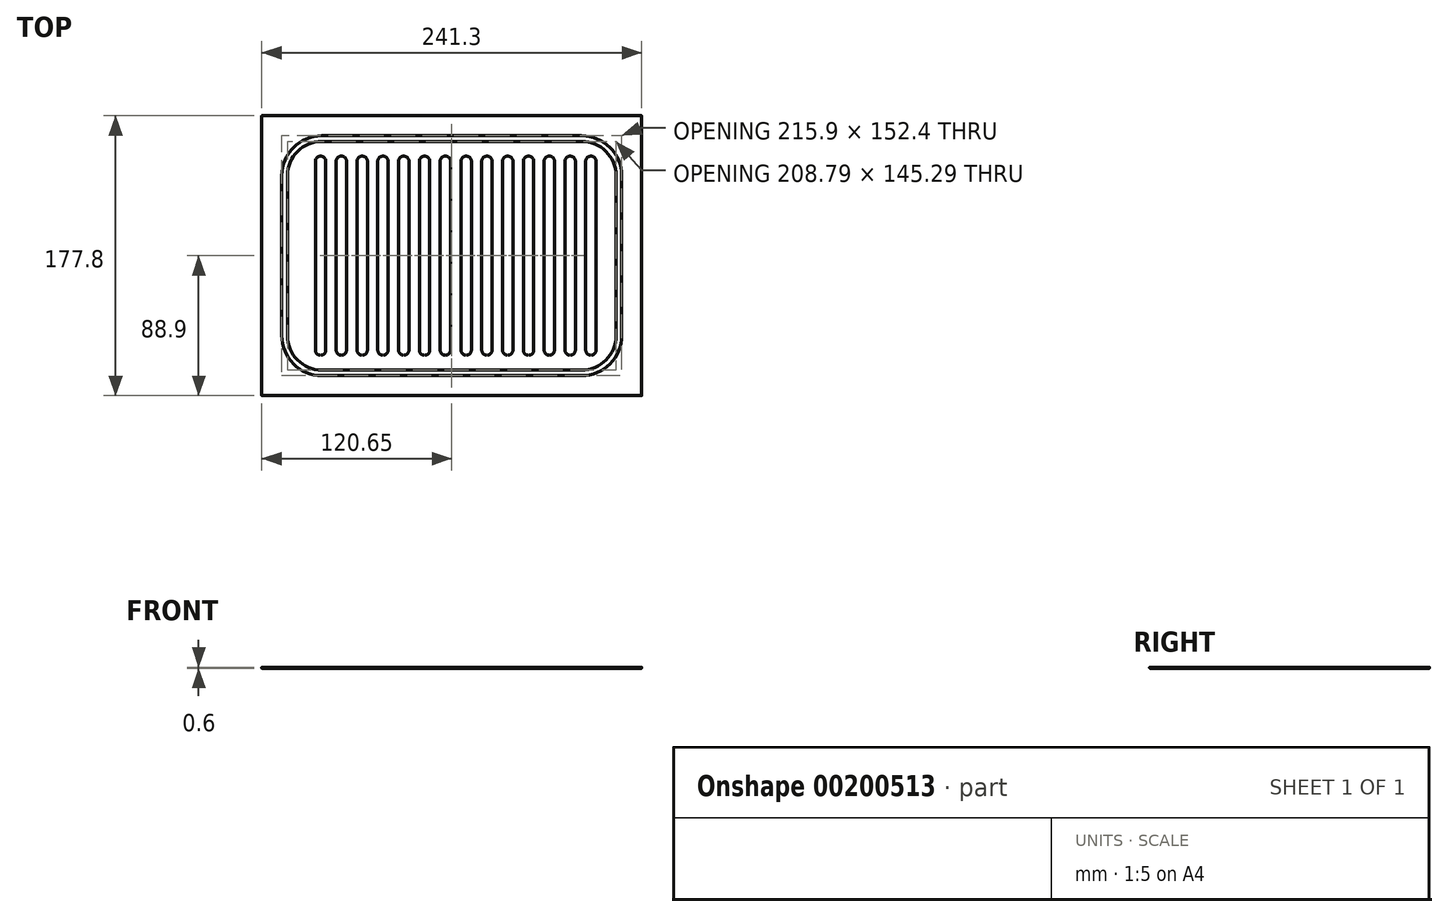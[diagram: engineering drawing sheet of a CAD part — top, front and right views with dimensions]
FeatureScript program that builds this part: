
annotation { "Feature Type Name" : "Feature", "Feature Type Description" : "" }
export const myFeature = defineFeature(function(context is Context, id is Id, definition is map)
    precondition{}
    {
        {
            var Q0;
            Q0=qCreatedBy(makeId("Top.planeOp"),FACE);
            var sketch = newSketch(context, id + "F0", { "sketchPlane" : qUnion([Q0])});
            skLineSegment(sketch, "E0.bottom", {"start": v(0, 177.8) * mm, "end": v(241.3, 177.8) * mm});
            skLineSegment(sketch, "E0.top", {"start": v(0, 0) * mm, "end": v(241.3, 0) * mm});
            skLineSegment(sketch, "E0.left", {"start": v(0, 177.8) * mm, "end": v(0, 0) * mm});
            skLineSegment(sketch, "E0.right", {"start": v(241.3, 177.8) * mm, "end": v(241.3, 0) * mm});
            skSolve(sketch);
        }
        {
            assignVariable(context, id + "F1", {"name" : "thickness", "anyValue" : .6});
        }
        {
            var Q0;
            Q0=makeQuery(id+"F0.imprint","IMPRINT",FACE,{"disambiguationData":[TD([[makeQuery(id+"F0.imprint","IMPRINT",EDGE,{"derivedFrom":sQuery(id+"F0.wireOp",EDGE,"E0.bottom")}),-1.0]])]});
            extrude(context, id + "F2", {"entities" : qUnion([Q0]), "depth" : (getVariable(context, 'thickness')) * mm});
        }
        {
            var Q0;
            Q0=makeQuery(id+"F2.opExtrude","CAP_FACE",FACE,{"disambiguationData":[OSD([sQuery(id+"F0.wireOp",EDGE,"E0.bottom"),sQuery(id+"F0.wireOp",EDGE,"E0.top"),sQuery(id+"F0.wireOp",EDGE,"E0.left"),sQuery(id+"F0.wireOp",EDGE,"E0.right"),sQuery(id+"F0.wireOp",EDGE,"lCrXFNj8-C2Ty-3Pfg-9sqa-s09L6QDRjWCV"),sQuery(id+"F0.wireOp",EDGE,"ff08c771-16cc-4d6c-ab3f-2ea9cd5ef540.0.1.0"),sQuery(id+"F0.wireOp",EDGE,"ff08c771-16cc-4d6c-ab3f-2ea9cd5ef540.0.2.0"),sQuery(id+"F0.wireOp",EDGE,"ff08c771-16cc-4d6c-ab3f-2ea9cd5ef540.1.0.0"),sQuery(id+"F0.wireOp",EDGE,"ff08c771-16cc-4d6c-ab3f-2ea9cd5ef540.1.1.0"),sQuery(id+"F0.wireOp",EDGE,"ff08c771-16cc-4d6c-ab3f-2ea9cd5ef540.1.2.0"),sQuery(id+"F0.wireOp",EDGE,"ff08c771-16cc-4d6c-ab3f-2ea9cd5ef540.2.0.0"),sQuery(id+"F0.wireOp",EDGE,"ff08c771-16cc-4d6c-ab3f-2ea9cd5ef540.2.1.0"),sQuery(id+"F0.wireOp",EDGE,"ff08c771-16cc-4d6c-ab3f-2ea9cd5ef540.2.2.0")])],"isStart":false});
            var sketch = newSketch(context, id + "F3", { "sketchPlane" : qUnion([Q0])});
            skLineSegment(sketch, "E1.0", {"start": v(203.2, 165.1) * mm, "end": v(38.1, 165.1) * mm});
            skLineSegment(sketch, "E1.1", {"start": v(228.6, 38.1) * mm, "end": v(228.6, 139.7) * mm});
            skLineSegment(sketch, "E1.2", {"start": v(38.1, 12.7) * mm, "end": v(203.2, 12.7) * mm});
            skLineSegment(sketch, "E1.3", {"start": v(12.7, 139.7) * mm, "end": v(12.7, 38.1) * mm});
            skArc(sketch, "E2.filletArc", {"start": v(38.1, 165.1) * mm, "mid": v(20.14, 157.66) * mm, "end": v(12.7, 139.7) * mm});
            skArc(sketch, "E3.filletArc", {"start": v(12.7, 38.1) * mm, "mid": v(20.14, 20.14) * mm, "end": v(38.1, 12.7) * mm});
            skArc(sketch, "E4.filletArc", {"start": v(203.2, 12.7) * mm, "mid": v(221.16, 20.14) * mm, "end": v(228.6, 38.1) * mm});
            skArc(sketch, "E5.filletArc", {"start": v(228.6, 139.7) * mm, "mid": v(221.16, 157.66) * mm, "end": v(203.2, 165.1) * mm});
            skLineSegment(sketch, "E6.0", {"start": v(16.26, 139.7) * mm, "end": v(16.26, 38.1) * mm});
            skLineSegment(sketch, "E7.0", {"start": v(38.1, 16.26) * mm, "end": v(203.2, 16.26) * mm});
            skLineSegment(sketch, "E8.0", {"start": v(225.04, 38.1) * mm, "end": v(225.04, 139.7) * mm});
            skLineSegment(sketch, "E9.0", {"start": v(203.2, 161.54) * mm, "end": v(38.1, 161.54) * mm});
            skArc(sketch, "E10.0", {"start": v(16.26, 38.1) * mm, "mid": v(22.65, 22.65) * mm, "end": v(38.1, 16.26) * mm});
            skArc(sketch, "E11.0", {"start": v(203.2, 16.26) * mm, "mid": v(218.65, 22.65) * mm, "end": v(225.04, 38.1) * mm});
            skArc(sketch, "E12.0", {"start": v(225.04, 139.7) * mm, "mid": v(218.65, 155.15) * mm, "end": v(203.2, 161.54) * mm});
            skArc(sketch, "E13.0", {"start": v(38.1, 161.54) * mm, "mid": v(22.65, 155.15) * mm, "end": v(16.26, 139.7) * mm});
            skSolve(sketch);
        }
        {
            assignVariable(context, id + "F4", {"name" : "groove_depth", "anyValue" : .15});
        }
        {
            var Q0;
            Q0=makeQuery(id+"F3.imprint","IMPRINT",FACE,{"disambiguationData":[TD([[makeQuery(id+"F3.imprint","IMPRINT",EDGE,{"derivedFrom":sQuery(id+"F3.wireOp",EDGE,"E1.0")}),1.0]])]});
            extrude(context, id + "F5", {"entities" : qUnion([Q0]), "operationType" : NewBodyOperationType.REMOVE, "oppositeDirection" : true, "depth" : (getVariable(context, 'groove_depth')) * mm});
        }
        {
            var Q0;
            Q0=makeQuery(id+"F2.opExtrude","CAP_FACE",FACE,{"disambiguationData":[OSD([sQuery(id+"F0.wireOp",EDGE,"E0.bottom"),sQuery(id+"F0.wireOp",EDGE,"E0.top"),sQuery(id+"F0.wireOp",EDGE,"E0.left"),sQuery(id+"F0.wireOp",EDGE,"E0.right")])],"isStart":true});
            var sketch = newSketch(context, id + "F6", { "sketchPlane" : qUnion([Q0])});
            skLineSegment(sketch, "E14.0", {"start": v(203.2, -12.7) * mm, "end": v(38.1, -12.7) * mm});
            skLineSegment(sketch, "E14.1", {"start": v(228.6, -139.7) * mm, "end": v(228.6, -38.1) * mm});
            skLineSegment(sketch, "E14.2", {"start": v(38.1, -165.1) * mm, "end": v(203.2, -165.1) * mm});
            skLineSegment(sketch, "E14.3", {"start": v(12.7, -38.1) * mm, "end": v(12.7, -139.7) * mm});
            skArc(sketch, "E15.filletArc", {"start": v(38.1, -12.7) * mm, "mid": v(20.14, -20.14) * mm, "end": v(12.7, -38.1) * mm});
            skArc(sketch, "E16.filletArc", {"start": v(12.7, -139.7) * mm, "mid": v(20.14, -157.66) * mm, "end": v(38.1, -165.1) * mm});
            skArc(sketch, "E17.filletArc", {"start": v(203.2, -165.1) * mm, "mid": v(221.16, -157.66) * mm, "end": v(228.6, -139.7) * mm});
            skArc(sketch, "E18.filletArc", {"start": v(228.6, -38.1) * mm, "mid": v(221.16, -20.14) * mm, "end": v(203.2, -12.7) * mm});
            skLineSegment(sketch, "E19.0", {"start": v(16.26, -38.1) * mm, "end": v(16.26, -139.7) * mm});
            skLineSegment(sketch, "E20.0", {"start": v(38.1, -161.54) * mm, "end": v(203.2, -161.54) * mm});
            skLineSegment(sketch, "E21.0", {"start": v(225.04, -139.7) * mm, "end": v(225.04, -38.1) * mm});
            skLineSegment(sketch, "E22.0", {"start": v(203.2, -16.26) * mm, "end": v(38.1, -16.26) * mm});
            skArc(sketch, "E23.0", {"start": v(16.26, -139.7) * mm, "mid": v(22.65, -155.15) * mm, "end": v(38.1, -161.54) * mm});
            skArc(sketch, "E24.0", {"start": v(203.2, -161.54) * mm, "mid": v(218.65, -155.15) * mm, "end": v(225.04, -139.7) * mm});
            skArc(sketch, "E25.0", {"start": v(225.04, -38.1) * mm, "mid": v(218.65, -22.65) * mm, "end": v(203.2, -16.26) * mm});
            skArc(sketch, "E26.0", {"start": v(38.1, -16.26) * mm, "mid": v(22.65, -22.65) * mm, "end": v(16.26, -38.1) * mm});
            skSolve(sketch);
        }
        {
            var Q0;
            Q0 = qSketchRegion(id + "F6", true);
            extrude(context, id + "F7", {"entities" : qUnion([Q0]), "operationType" : NewBodyOperationType.REMOVE, "oppositeDirection" : true, "depth" : (getVariable(context, 'groove_depth')) * mm});
        }
        {
            var Q0;
            Q0=makeQuery(id+"F2.opExtrude","CAP_FACE",FACE,{"disambiguationData":[OSD([sQuery(id+"F0.wireOp",EDGE,"E0.bottom"),sQuery(id+"F0.wireOp",EDGE,"E0.top"),sQuery(id+"F0.wireOp",EDGE,"E0.left"),sQuery(id+"F0.wireOp",EDGE,"E0.right")])],"isStart":true});
            var sketch = newSketch(context, id + "F8", { "sketchPlane" : qUnion([Q0])});
            skLineSegment(sketch, "E27", {"start": v(205.74, -148.84) * mm, "end": v(205.74, -28.96) * mm});
            skLineSegment(sketch, "E28.0", {"start": v(212.34, -148.84) * mm, "end": v(212.34, -28.96) * mm});
            skArc(sketch, "E29", {"start": v(212.34, -28.96) * mm, "mid": v(209.04, -25.65) * mm, "end": v(205.74, -28.96) * mm});
            skArc(sketch, "E30", {"start": v(205.74, -148.84) * mm, "mid": v(209.04, -152.15) * mm, "end": v(212.34, -148.84) * mm});
            skArc(sketch, "E31.1.0.0", {"start": v(199.14, -28.96) * mm, "mid": v(195.83, -25.65) * mm, "end": v(192.53, -28.96) * mm});
            skArc(sketch, "E31.1.0.1", {"start": v(192.53, -148.84) * mm, "mid": v(195.83, -152.15) * mm, "end": v(199.14, -148.84) * mm});
            skLineSegment(sketch, "E31.1.0.2", {"start": v(199.14, -148.84) * mm, "end": v(199.14, -28.96) * mm});
            skLineSegment(sketch, "E31.1.0.3", {"start": v(192.53, -148.84) * mm, "end": v(192.53, -28.96) * mm});
            skArc(sketch, "E31.2.0.0", {"start": v(185.93, -28.96) * mm, "mid": v(182.63, -25.65) * mm, "end": v(179.32, -28.96) * mm});
            skArc(sketch, "E31.2.0.1", {"start": v(179.32, -148.84) * mm, "mid": v(182.63, -152.15) * mm, "end": v(185.93, -148.84) * mm});
            skLineSegment(sketch, "E31.2.0.2", {"start": v(185.93, -148.84) * mm, "end": v(185.93, -28.96) * mm});
            skLineSegment(sketch, "E31.2.0.3", {"start": v(179.32, -148.84) * mm, "end": v(179.32, -28.96) * mm});
            skArc(sketch, "E31.3.0.0", {"start": v(172.72, -28.96) * mm, "mid": v(169.42, -25.65) * mm, "end": v(166.12, -28.96) * mm});
            skArc(sketch, "E31.3.0.1", {"start": v(166.12, -148.84) * mm, "mid": v(169.42, -152.15) * mm, "end": v(172.72, -148.84) * mm});
            skLineSegment(sketch, "E31.3.0.2", {"start": v(172.72, -148.84) * mm, "end": v(172.72, -28.96) * mm});
            skLineSegment(sketch, "E31.3.0.3", {"start": v(166.12, -148.84) * mm, "end": v(166.12, -28.96) * mm});
            skLineSegment(sketch, "E31.direction1", {"start": v(205.74, -148.84) * mm, "end": v(192.53, -148.84) * mm, "construction": true});
            skArc(sketch, "E32.0.4.0", {"start": v(159.51, -28.96) * mm, "mid": v(156.2, -25.65) * mm, "end": v(152.9, -28.96) * mm});
            skArc(sketch, "E32.4.4.0", {"start": v(152.9, -148.84) * mm, "mid": v(156.2, -152.15) * mm, "end": v(159.51, -148.84) * mm});
            skLineSegment(sketch, "E32.8.4.0", {"start": v(159.51, -148.84) * mm, "end": v(159.51, -28.96) * mm});
            skLineSegment(sketch, "E32.11.4.0", {"start": v(152.9, -148.84) * mm, "end": v(152.9, -28.96) * mm});
            skArc(sketch, "E32.0.5.0", {"start": v(146.3, -28.96) * mm, "mid": v(143, -25.65) * mm, "end": v(139.7, -28.96) * mm});
            skArc(sketch, "E32.4.5.0", {"start": v(139.7, -148.84) * mm, "mid": v(143, -152.15) * mm, "end": v(146.3, -148.84) * mm});
            skLineSegment(sketch, "E32.8.5.0", {"start": v(146.3, -148.84) * mm, "end": v(146.3, -28.96) * mm});
            skLineSegment(sketch, "E32.11.5.0", {"start": v(139.7, -148.84) * mm, "end": v(139.7, -28.96) * mm});
            skArc(sketch, "E32.0.6.0", {"start": v(133.1, -28.96) * mm, "mid": v(129.8, -25.65) * mm, "end": v(126.5, -28.96) * mm});
            skArc(sketch, "E32.4.6.0", {"start": v(126.5, -148.84) * mm, "mid": v(129.8, -152.15) * mm, "end": v(133.1, -148.84) * mm});
            skLineSegment(sketch, "E32.8.6.0", {"start": v(133.1, -148.84) * mm, "end": v(133.1, -28.96) * mm});
            skLineSegment(sketch, "E32.11.6.0", {"start": v(126.5, -148.84) * mm, "end": v(126.5, -28.96) * mm});
            skArc(sketch, "E32.0.7.0", {"start": v(119.89, -28.96) * mm, "mid": v(116.59, -25.65) * mm, "end": v(113.28, -28.96) * mm});
            skArc(sketch, "E32.4.7.0", {"start": v(113.28, -148.84) * mm, "mid": v(116.59, -152.15) * mm, "end": v(119.89, -148.84) * mm});
            skLineSegment(sketch, "E32.8.7.0", {"start": v(119.89, -148.84) * mm, "end": v(119.89, -28.96) * mm});
            skLineSegment(sketch, "E32.11.7.0", {"start": v(113.28, -148.84) * mm, "end": v(113.28, -28.96) * mm});
            skArc(sketch, "E32.0.8.0", {"start": v(106.68, -28.96) * mm, "mid": v(103.38, -25.65) * mm, "end": v(100.08, -28.96) * mm});
            skArc(sketch, "E32.4.8.0", {"start": v(100.08, -148.84) * mm, "mid": v(103.38, -152.15) * mm, "end": v(106.68, -148.84) * mm});
            skLineSegment(sketch, "E32.8.8.0", {"start": v(106.68, -148.84) * mm, "end": v(106.68, -28.96) * mm});
            skLineSegment(sketch, "E32.11.8.0", {"start": v(100.08, -148.84) * mm, "end": v(100.08, -28.96) * mm});
            skArc(sketch, "E32.0.9.0", {"start": v(93.47, -28.96) * mm, "mid": v(90.17, -25.65) * mm, "end": v(86.87, -28.96) * mm});
            skArc(sketch, "E32.4.9.0", {"start": v(86.87, -148.84) * mm, "mid": v(90.17, -152.15) * mm, "end": v(93.47, -148.84) * mm});
            skLineSegment(sketch, "E32.8.9.0", {"start": v(93.47, -148.84) * mm, "end": v(93.47, -28.96) * mm});
            skLineSegment(sketch, "E32.11.9.0", {"start": v(86.87, -148.84) * mm, "end": v(86.87, -28.96) * mm});
            skArc(sketch, "E32.0.10.0", {"start": v(80.26, -28.96) * mm, "mid": v(76.96, -25.65) * mm, "end": v(73.66, -28.96) * mm});
            skArc(sketch, "E32.4.10.0", {"start": v(73.66, -148.84) * mm, "mid": v(76.96, -152.15) * mm, "end": v(80.26, -148.84) * mm});
            skLineSegment(sketch, "E32.8.10.0", {"start": v(80.26, -148.84) * mm, "end": v(80.26, -28.96) * mm});
            skLineSegment(sketch, "E32.11.10.0", {"start": v(73.66, -148.84) * mm, "end": v(73.66, -28.96) * mm});
            skArc(sketch, "E32.0.11.0", {"start": v(67.06, -28.96) * mm, "mid": v(63.75, -25.65) * mm, "end": v(60.45, -28.96) * mm});
            skArc(sketch, "E32.4.11.0", {"start": v(60.45, -148.84) * mm, "mid": v(63.75, -152.15) * mm, "end": v(67.06, -148.84) * mm});
            skLineSegment(sketch, "E32.8.11.0", {"start": v(67.06, -148.84) * mm, "end": v(67.06, -28.96) * mm});
            skLineSegment(sketch, "E32.11.11.0", {"start": v(60.45, -148.84) * mm, "end": v(60.45, -28.96) * mm});
            skArc(sketch, "E33.0.12.0", {"start": v(53.85, -28.96) * mm, "mid": v(50.55, -25.65) * mm, "end": v(47.24, -28.96) * mm});
            skArc(sketch, "E33.4.12.0", {"start": v(47.24, -148.84) * mm, "mid": v(50.55, -152.15) * mm, "end": v(53.85, -148.84) * mm});
            skLineSegment(sketch, "E33.8.12.0", {"start": v(53.85, -148.84) * mm, "end": v(53.85, -28.96) * mm});
            skLineSegment(sketch, "E33.11.12.0", {"start": v(47.24, -148.84) * mm, "end": v(47.24, -28.96) * mm});
            skArc(sketch, "E33.0.13.0", {"start": v(40.64, -28.96) * mm, "mid": v(37.34, -25.65) * mm, "end": v(34.04, -28.96) * mm});
            skArc(sketch, "E33.4.13.0", {"start": v(34.04, -148.84) * mm, "mid": v(37.34, -152.15) * mm, "end": v(40.64, -148.84) * mm});
            skLineSegment(sketch, "E33.8.13.0", {"start": v(40.64, -148.84) * mm, "end": v(40.64, -28.96) * mm});
            skLineSegment(sketch, "E33.11.13.0", {"start": v(34.04, -148.84) * mm, "end": v(34.04, -28.96) * mm});
            skSolve(sketch);
        }
        {
            var Q0;
            Q0 = qSketchRegion(id + "F8", true);
            extrude(context, id + "F9", {"entities" : qUnion([Q0]), "operationType" : NewBodyOperationType.REMOVE, "endBound" : BoundingType.THROUGH_ALL, "oppositeDirection" : true, "depth" : 25.4 * mm});
        }
        {
            assignVariable(context, id + "F10", {"name" : "slot_radius", "anyValue" : 0.05});
        }
        {
            var Q0;
            Q0=makeQuery(id+"F9.boolean.opBoolean","INTERSECT",EDGE,{"derivedFrom":[makeQuery(id+"F5.boolean.opBoolean","SPLIT",FACE,{"disambiguationData":[TD([makeQuery(id+"F5.opExtrude","SWEPT_FACE",FACE,{"disambiguationData":[OSD([sQuery(id+"F3.wireOp",EDGE,"E6.0")])]})])],"derivedFrom":makeQuery(id+"F2.opExtrude","CAP_FACE",FACE,{"disambiguationData":[OSD([sQuery(id+"F0.wireOp",EDGE,"E0.bottom"),sQuery(id+"F0.wireOp",EDGE,"E0.top"),sQuery(id+"F0.wireOp",EDGE,"E0.left"),sQuery(id+"F0.wireOp",EDGE,"E0.right")])],"isStart":false})}),makeQuery(id+"F9.opExtrude","SWEPT_FACE",FACE,{"disambiguationData":[OSD([sQuery(id+"F8.wireOp",EDGE,"E33.11.13.0")])]})]});
            var Q1;
            Q1=makeQuery(id+"F9.boolean.opBoolean","INTERSECT",EDGE,{"derivedFrom":[makeQuery(id+"F5.boolean.opBoolean","SPLIT",FACE,{"disambiguationData":[TD([makeQuery(id+"F5.opExtrude","SWEPT_FACE",FACE,{"disambiguationData":[OSD([sQuery(id+"F3.wireOp",EDGE,"E6.0")])]})])],"derivedFrom":makeQuery(id+"F2.opExtrude","CAP_FACE",FACE,{"disambiguationData":[OSD([sQuery(id+"F0.wireOp",EDGE,"E0.bottom"),sQuery(id+"F0.wireOp",EDGE,"E0.top"),sQuery(id+"F0.wireOp",EDGE,"E0.left"),sQuery(id+"F0.wireOp",EDGE,"E0.right")])],"isStart":false})}),makeQuery(id+"F9.opExtrude","SWEPT_FACE",FACE,{"disambiguationData":[OSD([sQuery(id+"F8.wireOp",EDGE,"E33.8.13.0")])]})]});
            var Q2;
            Q2=makeQuery(id+"F9.boolean.opBoolean","INTERSECT",EDGE,{"derivedFrom":[makeQuery(id+"F5.boolean.opBoolean","SPLIT",FACE,{"disambiguationData":[TD([makeQuery(id+"F5.opExtrude","SWEPT_FACE",FACE,{"disambiguationData":[OSD([sQuery(id+"F3.wireOp",EDGE,"E6.0")])]})])],"derivedFrom":makeQuery(id+"F2.opExtrude","CAP_FACE",FACE,{"disambiguationData":[OSD([sQuery(id+"F0.wireOp",EDGE,"E0.bottom"),sQuery(id+"F0.wireOp",EDGE,"E0.top"),sQuery(id+"F0.wireOp",EDGE,"E0.left"),sQuery(id+"F0.wireOp",EDGE,"E0.right")])],"isStart":false})}),makeQuery(id+"F9.opExtrude","SWEPT_FACE",FACE,{"disambiguationData":[OSD([sQuery(id+"F8.wireOp",EDGE,"E33.11.12.0")])]})]});
            var Q3;
            Q3=makeQuery(id+"F9.boolean.opBoolean","INTERSECT",EDGE,{"derivedFrom":[makeQuery(id+"F5.boolean.opBoolean","SPLIT",FACE,{"disambiguationData":[TD([makeQuery(id+"F5.opExtrude","SWEPT_FACE",FACE,{"disambiguationData":[OSD([sQuery(id+"F3.wireOp",EDGE,"E6.0")])]})])],"derivedFrom":makeQuery(id+"F2.opExtrude","CAP_FACE",FACE,{"disambiguationData":[OSD([sQuery(id+"F0.wireOp",EDGE,"E0.bottom"),sQuery(id+"F0.wireOp",EDGE,"E0.top"),sQuery(id+"F0.wireOp",EDGE,"E0.left"),sQuery(id+"F0.wireOp",EDGE,"E0.right")])],"isStart":false})}),makeQuery(id+"F9.opExtrude","SWEPT_FACE",FACE,{"disambiguationData":[OSD([sQuery(id+"F8.wireOp",EDGE,"E33.8.12.0")])]})]});
            var Q4;
            Q4=makeQuery(id+"F9.boolean.opBoolean","INTERSECT",EDGE,{"derivedFrom":[makeQuery(id+"F5.boolean.opBoolean","SPLIT",FACE,{"disambiguationData":[TD([makeQuery(id+"F5.opExtrude","SWEPT_FACE",FACE,{"disambiguationData":[OSD([sQuery(id+"F3.wireOp",EDGE,"E6.0")])]})])],"derivedFrom":makeQuery(id+"F2.opExtrude","CAP_FACE",FACE,{"disambiguationData":[OSD([sQuery(id+"F0.wireOp",EDGE,"E0.bottom"),sQuery(id+"F0.wireOp",EDGE,"E0.top"),sQuery(id+"F0.wireOp",EDGE,"E0.left"),sQuery(id+"F0.wireOp",EDGE,"E0.right")])],"isStart":false})}),makeQuery(id+"F9.opExtrude","SWEPT_FACE",FACE,{"disambiguationData":[OSD([sQuery(id+"F8.wireOp",EDGE,"E32.11.11.0")])]})]});
            var Q5;
            Q5=makeQuery(id+"F9.boolean.opBoolean","INTERSECT",EDGE,{"derivedFrom":[makeQuery(id+"F5.boolean.opBoolean","SPLIT",FACE,{"disambiguationData":[TD([makeQuery(id+"F5.opExtrude","SWEPT_FACE",FACE,{"disambiguationData":[OSD([sQuery(id+"F3.wireOp",EDGE,"E6.0")])]})])],"derivedFrom":makeQuery(id+"F2.opExtrude","CAP_FACE",FACE,{"disambiguationData":[OSD([sQuery(id+"F0.wireOp",EDGE,"E0.bottom"),sQuery(id+"F0.wireOp",EDGE,"E0.top"),sQuery(id+"F0.wireOp",EDGE,"E0.left"),sQuery(id+"F0.wireOp",EDGE,"E0.right")])],"isStart":false})}),makeQuery(id+"F9.opExtrude","SWEPT_FACE",FACE,{"disambiguationData":[OSD([sQuery(id+"F8.wireOp",EDGE,"E32.8.11.0")])]})]});
            var Q6;
            Q6=makeQuery(id+"F9.boolean.opBoolean","INTERSECT",EDGE,{"derivedFrom":[makeQuery(id+"F5.boolean.opBoolean","SPLIT",FACE,{"disambiguationData":[TD([makeQuery(id+"F5.opExtrude","SWEPT_FACE",FACE,{"disambiguationData":[OSD([sQuery(id+"F3.wireOp",EDGE,"E6.0")])]})])],"derivedFrom":makeQuery(id+"F2.opExtrude","CAP_FACE",FACE,{"disambiguationData":[OSD([sQuery(id+"F0.wireOp",EDGE,"E0.bottom"),sQuery(id+"F0.wireOp",EDGE,"E0.top"),sQuery(id+"F0.wireOp",EDGE,"E0.left"),sQuery(id+"F0.wireOp",EDGE,"E0.right")])],"isStart":false})}),makeQuery(id+"F9.opExtrude","SWEPT_FACE",FACE,{"disambiguationData":[OSD([sQuery(id+"F8.wireOp",EDGE,"E32.11.10.0")])]})]});
            var Q7;
            Q7=makeQuery(id+"F9.boolean.opBoolean","INTERSECT",EDGE,{"derivedFrom":[makeQuery(id+"F5.boolean.opBoolean","SPLIT",FACE,{"disambiguationData":[TD([makeQuery(id+"F5.opExtrude","SWEPT_FACE",FACE,{"disambiguationData":[OSD([sQuery(id+"F3.wireOp",EDGE,"E6.0")])]})])],"derivedFrom":makeQuery(id+"F2.opExtrude","CAP_FACE",FACE,{"disambiguationData":[OSD([sQuery(id+"F0.wireOp",EDGE,"E0.bottom"),sQuery(id+"F0.wireOp",EDGE,"E0.top"),sQuery(id+"F0.wireOp",EDGE,"E0.left"),sQuery(id+"F0.wireOp",EDGE,"E0.right")])],"isStart":false})}),makeQuery(id+"F9.opExtrude","SWEPT_FACE",FACE,{"disambiguationData":[OSD([sQuery(id+"F8.wireOp",EDGE,"E32.8.10.0")])]})]});
            var Q8;
            Q8=makeQuery(id+"F9.boolean.opBoolean","INTERSECT",EDGE,{"derivedFrom":[makeQuery(id+"F5.boolean.opBoolean","SPLIT",FACE,{"disambiguationData":[TD([makeQuery(id+"F5.opExtrude","SWEPT_FACE",FACE,{"disambiguationData":[OSD([sQuery(id+"F3.wireOp",EDGE,"E6.0")])]})])],"derivedFrom":makeQuery(id+"F2.opExtrude","CAP_FACE",FACE,{"disambiguationData":[OSD([sQuery(id+"F0.wireOp",EDGE,"E0.bottom"),sQuery(id+"F0.wireOp",EDGE,"E0.top"),sQuery(id+"F0.wireOp",EDGE,"E0.left"),sQuery(id+"F0.wireOp",EDGE,"E0.right")])],"isStart":false})}),makeQuery(id+"F9.opExtrude","SWEPT_FACE",FACE,{"disambiguationData":[OSD([sQuery(id+"F8.wireOp",EDGE,"E32.11.9.0")])]})]});
            var Q9;
            Q9=makeQuery(id+"F9.boolean.opBoolean","INTERSECT",EDGE,{"derivedFrom":[makeQuery(id+"F5.boolean.opBoolean","SPLIT",FACE,{"disambiguationData":[TD([makeQuery(id+"F5.opExtrude","SWEPT_FACE",FACE,{"disambiguationData":[OSD([sQuery(id+"F3.wireOp",EDGE,"E6.0")])]})])],"derivedFrom":makeQuery(id+"F2.opExtrude","CAP_FACE",FACE,{"disambiguationData":[OSD([sQuery(id+"F0.wireOp",EDGE,"E0.bottom"),sQuery(id+"F0.wireOp",EDGE,"E0.top"),sQuery(id+"F0.wireOp",EDGE,"E0.left"),sQuery(id+"F0.wireOp",EDGE,"E0.right")])],"isStart":false})}),makeQuery(id+"F9.opExtrude","SWEPT_FACE",FACE,{"disambiguationData":[OSD([sQuery(id+"F8.wireOp",EDGE,"E32.8.9.0")])]})]});
            var Q10;
            Q10=makeQuery(id+"F9.boolean.opBoolean","INTERSECT",EDGE,{"derivedFrom":[makeQuery(id+"F5.boolean.opBoolean","SPLIT",FACE,{"disambiguationData":[TD([makeQuery(id+"F5.opExtrude","SWEPT_FACE",FACE,{"disambiguationData":[OSD([sQuery(id+"F3.wireOp",EDGE,"E6.0")])]})])],"derivedFrom":makeQuery(id+"F2.opExtrude","CAP_FACE",FACE,{"disambiguationData":[OSD([sQuery(id+"F0.wireOp",EDGE,"E0.bottom"),sQuery(id+"F0.wireOp",EDGE,"E0.top"),sQuery(id+"F0.wireOp",EDGE,"E0.left"),sQuery(id+"F0.wireOp",EDGE,"E0.right")])],"isStart":false})}),makeQuery(id+"F9.opExtrude","SWEPT_FACE",FACE,{"disambiguationData":[OSD([sQuery(id+"F8.wireOp",EDGE,"E32.11.8.0")])]})]});
            var Q11;
            Q11=makeQuery(id+"F9.boolean.opBoolean","INTERSECT",EDGE,{"derivedFrom":[makeQuery(id+"F5.boolean.opBoolean","SPLIT",FACE,{"disambiguationData":[TD([makeQuery(id+"F5.opExtrude","SWEPT_FACE",FACE,{"disambiguationData":[OSD([sQuery(id+"F3.wireOp",EDGE,"E6.0")])]})])],"derivedFrom":makeQuery(id+"F2.opExtrude","CAP_FACE",FACE,{"disambiguationData":[OSD([sQuery(id+"F0.wireOp",EDGE,"E0.bottom"),sQuery(id+"F0.wireOp",EDGE,"E0.top"),sQuery(id+"F0.wireOp",EDGE,"E0.left"),sQuery(id+"F0.wireOp",EDGE,"E0.right")])],"isStart":false})}),makeQuery(id+"F9.opExtrude","SWEPT_FACE",FACE,{"disambiguationData":[OSD([sQuery(id+"F8.wireOp",EDGE,"E32.8.8.0")])]})]});
            var Q12;
            Q12=makeQuery(id+"F9.boolean.opBoolean","INTERSECT",EDGE,{"derivedFrom":[makeQuery(id+"F5.boolean.opBoolean","SPLIT",FACE,{"disambiguationData":[TD([makeQuery(id+"F5.opExtrude","SWEPT_FACE",FACE,{"disambiguationData":[OSD([sQuery(id+"F3.wireOp",EDGE,"E6.0")])]})])],"derivedFrom":makeQuery(id+"F2.opExtrude","CAP_FACE",FACE,{"disambiguationData":[OSD([sQuery(id+"F0.wireOp",EDGE,"E0.bottom"),sQuery(id+"F0.wireOp",EDGE,"E0.top"),sQuery(id+"F0.wireOp",EDGE,"E0.left"),sQuery(id+"F0.wireOp",EDGE,"E0.right")])],"isStart":false})}),makeQuery(id+"F9.opExtrude","SWEPT_FACE",FACE,{"disambiguationData":[OSD([sQuery(id+"F8.wireOp",EDGE,"E32.11.7.0")])]})]});
            var Q13;
            Q13=makeQuery(id+"F9.boolean.opBoolean","INTERSECT",EDGE,{"derivedFrom":[makeQuery(id+"F5.boolean.opBoolean","SPLIT",FACE,{"disambiguationData":[TD([makeQuery(id+"F5.opExtrude","SWEPT_FACE",FACE,{"disambiguationData":[OSD([sQuery(id+"F3.wireOp",EDGE,"E6.0")])]})])],"derivedFrom":makeQuery(id+"F2.opExtrude","CAP_FACE",FACE,{"disambiguationData":[OSD([sQuery(id+"F0.wireOp",EDGE,"E0.bottom"),sQuery(id+"F0.wireOp",EDGE,"E0.top"),sQuery(id+"F0.wireOp",EDGE,"E0.left"),sQuery(id+"F0.wireOp",EDGE,"E0.right")])],"isStart":false})}),makeQuery(id+"F9.opExtrude","SWEPT_FACE",FACE,{"disambiguationData":[OSD([sQuery(id+"F8.wireOp",EDGE,"E32.8.7.0")])]})]});
            var Q14;
            Q14=makeQuery(id+"F9.boolean.opBoolean","INTERSECT",EDGE,{"derivedFrom":[makeQuery(id+"F5.boolean.opBoolean","SPLIT",FACE,{"disambiguationData":[TD([makeQuery(id+"F5.opExtrude","SWEPT_FACE",FACE,{"disambiguationData":[OSD([sQuery(id+"F3.wireOp",EDGE,"E6.0")])]})])],"derivedFrom":makeQuery(id+"F2.opExtrude","CAP_FACE",FACE,{"disambiguationData":[OSD([sQuery(id+"F0.wireOp",EDGE,"E0.bottom"),sQuery(id+"F0.wireOp",EDGE,"E0.top"),sQuery(id+"F0.wireOp",EDGE,"E0.left"),sQuery(id+"F0.wireOp",EDGE,"E0.right")])],"isStart":false})}),makeQuery(id+"F9.opExtrude","SWEPT_FACE",FACE,{"disambiguationData":[OSD([sQuery(id+"F8.wireOp",EDGE,"E32.11.6.0")])]})]});
            var Q15;
            Q15=makeQuery(id+"F9.boolean.opBoolean","INTERSECT",EDGE,{"derivedFrom":[makeQuery(id+"F5.boolean.opBoolean","SPLIT",FACE,{"disambiguationData":[TD([makeQuery(id+"F5.opExtrude","SWEPT_FACE",FACE,{"disambiguationData":[OSD([sQuery(id+"F3.wireOp",EDGE,"E6.0")])]})])],"derivedFrom":makeQuery(id+"F2.opExtrude","CAP_FACE",FACE,{"disambiguationData":[OSD([sQuery(id+"F0.wireOp",EDGE,"E0.bottom"),sQuery(id+"F0.wireOp",EDGE,"E0.top"),sQuery(id+"F0.wireOp",EDGE,"E0.left"),sQuery(id+"F0.wireOp",EDGE,"E0.right")])],"isStart":false})}),makeQuery(id+"F9.opExtrude","SWEPT_FACE",FACE,{"disambiguationData":[OSD([sQuery(id+"F8.wireOp",EDGE,"E32.8.6.0")])]})]});
            var Q16;
            Q16=makeQuery(id+"F9.boolean.opBoolean","INTERSECT",EDGE,{"derivedFrom":[makeQuery(id+"F5.boolean.opBoolean","SPLIT",FACE,{"disambiguationData":[TD([makeQuery(id+"F5.opExtrude","SWEPT_FACE",FACE,{"disambiguationData":[OSD([sQuery(id+"F3.wireOp",EDGE,"E6.0")])]})])],"derivedFrom":makeQuery(id+"F2.opExtrude","CAP_FACE",FACE,{"disambiguationData":[OSD([sQuery(id+"F0.wireOp",EDGE,"E0.bottom"),sQuery(id+"F0.wireOp",EDGE,"E0.top"),sQuery(id+"F0.wireOp",EDGE,"E0.left"),sQuery(id+"F0.wireOp",EDGE,"E0.right")])],"isStart":false})}),makeQuery(id+"F9.opExtrude","SWEPT_FACE",FACE,{"disambiguationData":[OSD([sQuery(id+"F8.wireOp",EDGE,"E32.11.5.0")])]})]});
            var Q17;
            Q17=makeQuery(id+"F9.boolean.opBoolean","INTERSECT",EDGE,{"derivedFrom":[makeQuery(id+"F5.boolean.opBoolean","SPLIT",FACE,{"disambiguationData":[TD([makeQuery(id+"F5.opExtrude","SWEPT_FACE",FACE,{"disambiguationData":[OSD([sQuery(id+"F3.wireOp",EDGE,"E6.0")])]})])],"derivedFrom":makeQuery(id+"F2.opExtrude","CAP_FACE",FACE,{"disambiguationData":[OSD([sQuery(id+"F0.wireOp",EDGE,"E0.bottom"),sQuery(id+"F0.wireOp",EDGE,"E0.top"),sQuery(id+"F0.wireOp",EDGE,"E0.left"),sQuery(id+"F0.wireOp",EDGE,"E0.right")])],"isStart":false})}),makeQuery(id+"F9.opExtrude","SWEPT_FACE",FACE,{"disambiguationData":[OSD([sQuery(id+"F8.wireOp",EDGE,"E32.8.5.0")])]})]});
            var Q18;
            Q18=makeQuery(id+"F9.boolean.opBoolean","INTERSECT",EDGE,{"derivedFrom":[makeQuery(id+"F5.boolean.opBoolean","SPLIT",FACE,{"disambiguationData":[TD([makeQuery(id+"F5.opExtrude","SWEPT_FACE",FACE,{"disambiguationData":[OSD([sQuery(id+"F3.wireOp",EDGE,"E6.0")])]})])],"derivedFrom":makeQuery(id+"F2.opExtrude","CAP_FACE",FACE,{"disambiguationData":[OSD([sQuery(id+"F0.wireOp",EDGE,"E0.bottom"),sQuery(id+"F0.wireOp",EDGE,"E0.top"),sQuery(id+"F0.wireOp",EDGE,"E0.left"),sQuery(id+"F0.wireOp",EDGE,"E0.right")])],"isStart":false})}),makeQuery(id+"F9.opExtrude","SWEPT_FACE",FACE,{"disambiguationData":[OSD([sQuery(id+"F8.wireOp",EDGE,"E32.11.4.0")])]})]});
            var Q19;
            Q19=makeQuery(id+"F9.boolean.opBoolean","INTERSECT",EDGE,{"derivedFrom":[makeQuery(id+"F5.boolean.opBoolean","SPLIT",FACE,{"disambiguationData":[TD([makeQuery(id+"F5.opExtrude","SWEPT_FACE",FACE,{"disambiguationData":[OSD([sQuery(id+"F3.wireOp",EDGE,"E6.0")])]})])],"derivedFrom":makeQuery(id+"F2.opExtrude","CAP_FACE",FACE,{"disambiguationData":[OSD([sQuery(id+"F0.wireOp",EDGE,"E0.bottom"),sQuery(id+"F0.wireOp",EDGE,"E0.top"),sQuery(id+"F0.wireOp",EDGE,"E0.left"),sQuery(id+"F0.wireOp",EDGE,"E0.right")])],"isStart":false})}),makeQuery(id+"F9.opExtrude","SWEPT_FACE",FACE,{"disambiguationData":[OSD([sQuery(id+"F8.wireOp",EDGE,"E32.8.4.0")])]})]});
            var Q20;
            Q20=makeQuery(id+"F9.boolean.opBoolean","INTERSECT",EDGE,{"derivedFrom":[makeQuery(id+"F5.boolean.opBoolean","SPLIT",FACE,{"disambiguationData":[TD([makeQuery(id+"F5.opExtrude","SWEPT_FACE",FACE,{"disambiguationData":[OSD([sQuery(id+"F3.wireOp",EDGE,"E6.0")])]})])],"derivedFrom":makeQuery(id+"F2.opExtrude","CAP_FACE",FACE,{"disambiguationData":[OSD([sQuery(id+"F0.wireOp",EDGE,"E0.bottom"),sQuery(id+"F0.wireOp",EDGE,"E0.top"),sQuery(id+"F0.wireOp",EDGE,"E0.left"),sQuery(id+"F0.wireOp",EDGE,"E0.right")])],"isStart":false})}),makeQuery(id+"F9.opExtrude","SWEPT_FACE",FACE,{"disambiguationData":[OSD([sQuery(id+"F8.wireOp",EDGE,"E31.3.0.3")])]})]});
            var Q21;
            Q21=makeQuery(id+"F9.boolean.opBoolean","INTERSECT",EDGE,{"derivedFrom":[makeQuery(id+"F5.boolean.opBoolean","SPLIT",FACE,{"disambiguationData":[TD([makeQuery(id+"F5.opExtrude","SWEPT_FACE",FACE,{"disambiguationData":[OSD([sQuery(id+"F3.wireOp",EDGE,"E6.0")])]})])],"derivedFrom":makeQuery(id+"F2.opExtrude","CAP_FACE",FACE,{"disambiguationData":[OSD([sQuery(id+"F0.wireOp",EDGE,"E0.bottom"),sQuery(id+"F0.wireOp",EDGE,"E0.top"),sQuery(id+"F0.wireOp",EDGE,"E0.left"),sQuery(id+"F0.wireOp",EDGE,"E0.right")])],"isStart":false})}),makeQuery(id+"F9.opExtrude","SWEPT_FACE",FACE,{"disambiguationData":[OSD([sQuery(id+"F8.wireOp",EDGE,"E31.3.0.2")])]})]});
            var Q22;
            Q22=makeQuery(id+"F9.boolean.opBoolean","INTERSECT",EDGE,{"derivedFrom":[makeQuery(id+"F5.boolean.opBoolean","SPLIT",FACE,{"disambiguationData":[TD([makeQuery(id+"F5.opExtrude","SWEPT_FACE",FACE,{"disambiguationData":[OSD([sQuery(id+"F3.wireOp",EDGE,"E6.0")])]})])],"derivedFrom":makeQuery(id+"F2.opExtrude","CAP_FACE",FACE,{"disambiguationData":[OSD([sQuery(id+"F0.wireOp",EDGE,"E0.bottom"),sQuery(id+"F0.wireOp",EDGE,"E0.top"),sQuery(id+"F0.wireOp",EDGE,"E0.left"),sQuery(id+"F0.wireOp",EDGE,"E0.right")])],"isStart":false})}),makeQuery(id+"F9.opExtrude","SWEPT_FACE",FACE,{"disambiguationData":[OSD([sQuery(id+"F8.wireOp",EDGE,"E31.2.0.3")])]})]});
            var Q23;
            Q23=makeQuery(id+"F9.boolean.opBoolean","INTERSECT",EDGE,{"derivedFrom":[makeQuery(id+"F5.boolean.opBoolean","SPLIT",FACE,{"disambiguationData":[TD([makeQuery(id+"F5.opExtrude","SWEPT_FACE",FACE,{"disambiguationData":[OSD([sQuery(id+"F3.wireOp",EDGE,"E6.0")])]})])],"derivedFrom":makeQuery(id+"F2.opExtrude","CAP_FACE",FACE,{"disambiguationData":[OSD([sQuery(id+"F0.wireOp",EDGE,"E0.bottom"),sQuery(id+"F0.wireOp",EDGE,"E0.top"),sQuery(id+"F0.wireOp",EDGE,"E0.left"),sQuery(id+"F0.wireOp",EDGE,"E0.right")])],"isStart":false})}),makeQuery(id+"F9.opExtrude","SWEPT_FACE",FACE,{"disambiguationData":[OSD([sQuery(id+"F8.wireOp",EDGE,"E31.2.0.2")])]})]});
            var Q24;
            Q24=makeQuery(id+"F9.boolean.opBoolean","INTERSECT",EDGE,{"derivedFrom":[makeQuery(id+"F5.boolean.opBoolean","SPLIT",FACE,{"disambiguationData":[TD([makeQuery(id+"F5.opExtrude","SWEPT_FACE",FACE,{"disambiguationData":[OSD([sQuery(id+"F3.wireOp",EDGE,"E6.0")])]})])],"derivedFrom":makeQuery(id+"F2.opExtrude","CAP_FACE",FACE,{"disambiguationData":[OSD([sQuery(id+"F0.wireOp",EDGE,"E0.bottom"),sQuery(id+"F0.wireOp",EDGE,"E0.top"),sQuery(id+"F0.wireOp",EDGE,"E0.left"),sQuery(id+"F0.wireOp",EDGE,"E0.right")])],"isStart":false})}),makeQuery(id+"F9.opExtrude","SWEPT_FACE",FACE,{"disambiguationData":[OSD([sQuery(id+"F8.wireOp",EDGE,"E31.1.0.3")])]})]});
            var Q25;
            Q25=makeQuery(id+"F9.boolean.opBoolean","INTERSECT",EDGE,{"derivedFrom":[makeQuery(id+"F5.boolean.opBoolean","SPLIT",FACE,{"disambiguationData":[TD([makeQuery(id+"F5.opExtrude","SWEPT_FACE",FACE,{"disambiguationData":[OSD([sQuery(id+"F3.wireOp",EDGE,"E6.0")])]})])],"derivedFrom":makeQuery(id+"F2.opExtrude","CAP_FACE",FACE,{"disambiguationData":[OSD([sQuery(id+"F0.wireOp",EDGE,"E0.bottom"),sQuery(id+"F0.wireOp",EDGE,"E0.top"),sQuery(id+"F0.wireOp",EDGE,"E0.left"),sQuery(id+"F0.wireOp",EDGE,"E0.right")])],"isStart":false})}),makeQuery(id+"F9.opExtrude","SWEPT_FACE",FACE,{"disambiguationData":[OSD([sQuery(id+"F8.wireOp",EDGE,"E31.1.0.2")])]})]});
            var Q26;
            Q26=makeQuery(id+"F9.boolean.opBoolean","INTERSECT",EDGE,{"derivedFrom":[makeQuery(id+"F5.boolean.opBoolean","SPLIT",FACE,{"disambiguationData":[TD([makeQuery(id+"F5.opExtrude","SWEPT_FACE",FACE,{"disambiguationData":[OSD([sQuery(id+"F3.wireOp",EDGE,"E6.0")])]})])],"derivedFrom":makeQuery(id+"F2.opExtrude","CAP_FACE",FACE,{"disambiguationData":[OSD([sQuery(id+"F0.wireOp",EDGE,"E0.bottom"),sQuery(id+"F0.wireOp",EDGE,"E0.top"),sQuery(id+"F0.wireOp",EDGE,"E0.left"),sQuery(id+"F0.wireOp",EDGE,"E0.right")])],"isStart":false})}),makeQuery(id+"F9.opExtrude","SWEPT_FACE",FACE,{"disambiguationData":[OSD([sQuery(id+"F8.wireOp",EDGE,"E27")])]})]});
            var Q27;
            Q27=makeQuery(id+"F9.boolean.opBoolean","INTERSECT",EDGE,{"derivedFrom":[makeQuery(id+"F5.boolean.opBoolean","SPLIT",FACE,{"disambiguationData":[TD([makeQuery(id+"F5.opExtrude","SWEPT_FACE",FACE,{"disambiguationData":[OSD([sQuery(id+"F3.wireOp",EDGE,"E6.0")])]})])],"derivedFrom":makeQuery(id+"F2.opExtrude","CAP_FACE",FACE,{"disambiguationData":[OSD([sQuery(id+"F0.wireOp",EDGE,"E0.bottom"),sQuery(id+"F0.wireOp",EDGE,"E0.top"),sQuery(id+"F0.wireOp",EDGE,"E0.left"),sQuery(id+"F0.wireOp",EDGE,"E0.right")])],"isStart":false})}),makeQuery(id+"F9.opExtrude","SWEPT_FACE",FACE,{"disambiguationData":[OSD([sQuery(id+"F8.wireOp",EDGE,"E28.0")])]})]});
            var Q28;
            Q28=makeQuery(id+"F2.opExtrude","CAP_EDGE",EDGE,{"disambiguationData":[OSD([sQuery(id+"F0.wireOp",EDGE,"E0.top")])],"isStart":true});
            var Q29;
            Q29=makeQuery(id+"F9.boolean.opBoolean","COPY",EDGE,{"derivedFrom":makeQuery(id+"F9.opExtrude","CAP_EDGE",EDGE,{"disambiguationData":[OSD([sQuery(id+"F8.wireOp",EDGE,"E33.11.13.0")])],"isStart":true})});
            var Q30;
            Q30=makeQuery(id+"F9.boolean.opBoolean","COPY",EDGE,{"derivedFrom":makeQuery(id+"F9.opExtrude","CAP_EDGE",EDGE,{"disambiguationData":[OSD([sQuery(id+"F8.wireOp",EDGE,"E33.8.13.0")])],"isStart":true})});
            var Q31;
            Q31=makeQuery(id+"F9.boolean.opBoolean","COPY",EDGE,{"derivedFrom":makeQuery(id+"F9.opExtrude","CAP_EDGE",EDGE,{"disambiguationData":[OSD([sQuery(id+"F8.wireOp",EDGE,"E33.11.12.0")])],"isStart":true})});
            var Q32;
            Q32=makeQuery(id+"F9.boolean.opBoolean","COPY",EDGE,{"derivedFrom":makeQuery(id+"F9.opExtrude","CAP_EDGE",EDGE,{"disambiguationData":[OSD([sQuery(id+"F8.wireOp",EDGE,"E33.8.12.0")])],"isStart":true})});
            var Q33;
            Q33=makeQuery(id+"F9.boolean.opBoolean","COPY",EDGE,{"derivedFrom":makeQuery(id+"F9.opExtrude","CAP_EDGE",EDGE,{"disambiguationData":[OSD([sQuery(id+"F8.wireOp",EDGE,"E32.11.11.0")])],"isStart":true})});
            var Q34;
            Q34=makeQuery(id+"F9.boolean.opBoolean","COPY",EDGE,{"derivedFrom":makeQuery(id+"F9.opExtrude","CAP_EDGE",EDGE,{"disambiguationData":[OSD([sQuery(id+"F8.wireOp",EDGE,"E32.8.11.0")])],"isStart":true})});
            var Q35;
            Q35=makeQuery(id+"F9.boolean.opBoolean","COPY",EDGE,{"derivedFrom":makeQuery(id+"F9.opExtrude","CAP_EDGE",EDGE,{"disambiguationData":[OSD([sQuery(id+"F8.wireOp",EDGE,"E32.11.10.0")])],"isStart":true})});
            var Q36;
            Q36=makeQuery(id+"F9.boolean.opBoolean","COPY",EDGE,{"derivedFrom":makeQuery(id+"F9.opExtrude","CAP_EDGE",EDGE,{"disambiguationData":[OSD([sQuery(id+"F8.wireOp",EDGE,"E32.8.10.0")])],"isStart":true})});
            var Q37;
            Q37=makeQuery(id+"F9.boolean.opBoolean","COPY",EDGE,{"derivedFrom":makeQuery(id+"F9.opExtrude","CAP_EDGE",EDGE,{"disambiguationData":[OSD([sQuery(id+"F8.wireOp",EDGE,"E32.11.9.0")])],"isStart":true})});
            var Q38;
            Q38=makeQuery(id+"F9.boolean.opBoolean","COPY",EDGE,{"derivedFrom":makeQuery(id+"F9.opExtrude","CAP_EDGE",EDGE,{"disambiguationData":[OSD([sQuery(id+"F8.wireOp",EDGE,"E32.8.9.0")])],"isStart":true})});
            var Q39;
            Q39=makeQuery(id+"F9.boolean.opBoolean","COPY",EDGE,{"derivedFrom":makeQuery(id+"F9.opExtrude","CAP_EDGE",EDGE,{"disambiguationData":[OSD([sQuery(id+"F8.wireOp",EDGE,"E32.11.8.0")])],"isStart":true})});
            var Q40;
            Q40=makeQuery(id+"F9.boolean.opBoolean","COPY",EDGE,{"derivedFrom":makeQuery(id+"F9.opExtrude","CAP_EDGE",EDGE,{"disambiguationData":[OSD([sQuery(id+"F8.wireOp",EDGE,"E32.8.8.0")])],"isStart":true})});
            var Q41;
            Q41=makeQuery(id+"F9.boolean.opBoolean","COPY",EDGE,{"derivedFrom":makeQuery(id+"F9.opExtrude","CAP_EDGE",EDGE,{"disambiguationData":[OSD([sQuery(id+"F8.wireOp",EDGE,"E32.11.7.0")])],"isStart":true})});
            var Q42;
            Q42=makeQuery(id+"F9.boolean.opBoolean","COPY",EDGE,{"derivedFrom":makeQuery(id+"F9.opExtrude","CAP_EDGE",EDGE,{"disambiguationData":[OSD([sQuery(id+"F8.wireOp",EDGE,"E32.8.7.0")])],"isStart":true})});
            var Q43;
            Q43=makeQuery(id+"F9.boolean.opBoolean","COPY",EDGE,{"derivedFrom":makeQuery(id+"F9.opExtrude","CAP_EDGE",EDGE,{"disambiguationData":[OSD([sQuery(id+"F8.wireOp",EDGE,"E32.11.6.0")])],"isStart":true})});
            var Q44;
            Q44=makeQuery(id+"F9.boolean.opBoolean","COPY",EDGE,{"derivedFrom":makeQuery(id+"F9.opExtrude","CAP_EDGE",EDGE,{"disambiguationData":[OSD([sQuery(id+"F8.wireOp",EDGE,"E32.8.6.0")])],"isStart":true})});
            var Q45;
            Q45=makeQuery(id+"F9.boolean.opBoolean","COPY",EDGE,{"derivedFrom":makeQuery(id+"F9.opExtrude","CAP_EDGE",EDGE,{"disambiguationData":[OSD([sQuery(id+"F8.wireOp",EDGE,"E32.11.5.0")])],"isStart":true})});
            var Q46;
            Q46=makeQuery(id+"F9.boolean.opBoolean","COPY",EDGE,{"derivedFrom":makeQuery(id+"F9.opExtrude","CAP_EDGE",EDGE,{"disambiguationData":[OSD([sQuery(id+"F8.wireOp",EDGE,"E32.8.5.0")])],"isStart":true})});
            var Q47;
            Q47=makeQuery(id+"F9.boolean.opBoolean","COPY",EDGE,{"derivedFrom":makeQuery(id+"F9.opExtrude","CAP_EDGE",EDGE,{"disambiguationData":[OSD([sQuery(id+"F8.wireOp",EDGE,"E32.11.4.0")])],"isStart":true})});
            var Q48;
            Q48=makeQuery(id+"F9.boolean.opBoolean","COPY",EDGE,{"derivedFrom":makeQuery(id+"F9.opExtrude","CAP_EDGE",EDGE,{"disambiguationData":[OSD([sQuery(id+"F8.wireOp",EDGE,"E32.8.4.0")])],"isStart":true})});
            var Q49;
            Q49=makeQuery(id+"F9.boolean.opBoolean","COPY",EDGE,{"derivedFrom":makeQuery(id+"F9.opExtrude","CAP_EDGE",EDGE,{"disambiguationData":[OSD([sQuery(id+"F8.wireOp",EDGE,"E31.3.0.3")])],"isStart":true})});
            var Q50;
            Q50=makeQuery(id+"F9.boolean.opBoolean","COPY",EDGE,{"derivedFrom":makeQuery(id+"F9.opExtrude","CAP_EDGE",EDGE,{"disambiguationData":[OSD([sQuery(id+"F8.wireOp",EDGE,"E31.3.0.2")])],"isStart":true})});
            var Q51;
            Q51=makeQuery(id+"F9.boolean.opBoolean","COPY",EDGE,{"derivedFrom":makeQuery(id+"F9.opExtrude","CAP_EDGE",EDGE,{"disambiguationData":[OSD([sQuery(id+"F8.wireOp",EDGE,"E31.2.0.3")])],"isStart":true})});
            var Q52;
            Q52=makeQuery(id+"F9.boolean.opBoolean","COPY",EDGE,{"derivedFrom":makeQuery(id+"F9.opExtrude","CAP_EDGE",EDGE,{"disambiguationData":[OSD([sQuery(id+"F8.wireOp",EDGE,"E31.2.0.2")])],"isStart":true})});
            var Q53;
            Q53=makeQuery(id+"F9.boolean.opBoolean","COPY",EDGE,{"derivedFrom":makeQuery(id+"F9.opExtrude","CAP_EDGE",EDGE,{"disambiguationData":[OSD([sQuery(id+"F8.wireOp",EDGE,"E31.1.0.3")])],"isStart":true})});
            var Q54;
            Q54=makeQuery(id+"F9.boolean.opBoolean","COPY",EDGE,{"derivedFrom":makeQuery(id+"F9.opExtrude","CAP_EDGE",EDGE,{"disambiguationData":[OSD([sQuery(id+"F8.wireOp",EDGE,"E31.1.0.2")])],"isStart":true})});
            var Q55;
            Q55=makeQuery(id+"F9.boolean.opBoolean","COPY",EDGE,{"derivedFrom":makeQuery(id+"F9.opExtrude","CAP_EDGE",EDGE,{"disambiguationData":[OSD([sQuery(id+"F8.wireOp",EDGE,"E27")])],"isStart":true})});
            var Q56;
            Q56=makeQuery(id+"F9.boolean.opBoolean","COPY",EDGE,{"derivedFrom":makeQuery(id+"F9.opExtrude","CAP_EDGE",EDGE,{"disambiguationData":[OSD([sQuery(id+"F8.wireOp",EDGE,"E28.0")])],"isStart":true})});
            fillet(context, id + "F11", {"entities" : qUnion([Q0, Q1, Q2, Q3, Q4, Q5, Q6, Q7, Q8, Q9, Q10, Q11, Q12, Q13, Q14, Q15, Q16, Q17, Q18, Q19, Q20, Q21, Q22, Q23, Q24, Q25, Q26, Q27, Q28, Q29, Q30, Q31, Q32, Q33, Q34, Q35, Q36, Q37, Q38, Q39, Q40, Q41, Q42, Q43, Q44, Q45, Q46, Q47, Q48, Q49, Q50, Q51, Q52, Q53, Q54, Q55, Q56]), "radius" : (getVariable(context, 'slot_radius')) * mm, "tangentPropagation" : true, "allowEdgeOverflow" : false});
        }
        {
            var Q0;
            Q0=makeQuery(id+"F2.opExtrude","CAP_EDGE",EDGE,{"disambiguationData":[OSD([sQuery(id+"F0.wireOp",EDGE,"E0.left")])],"isStart":false});
            var Q1;
            Q1=makeQuery(id+"F2.opExtrude","CAP_EDGE",EDGE,{"disambiguationData":[OSD([sQuery(id+"F0.wireOp",EDGE,"E0.bottom")])],"isStart":false});
            var Q2;
            Q2=makeQuery(id+"F2.opExtrude","CAP_EDGE",EDGE,{"disambiguationData":[OSD([sQuery(id+"F0.wireOp",EDGE,"E0.right")])],"isStart":false});
            var Q3;
            Q3=makeQuery(id+"F2.opExtrude","CAP_EDGE",EDGE,{"disambiguationData":[OSD([sQuery(id+"F0.wireOp",EDGE,"E0.top")])],"isStart":false});
            var Q4;
            Q4=makeQuery(id+"F2.opExtrude","CAP_EDGE",EDGE,{"disambiguationData":[OSD([sQuery(id+"F0.wireOp",EDGE,"E0.left")])],"isStart":true});
            var Q5;
            Q5=makeQuery(id+"F2.opExtrude","CAP_EDGE",EDGE,{"disambiguationData":[OSD([sQuery(id+"F0.wireOp",EDGE,"E0.bottom")])],"isStart":true});
            var Q6;
            {var subQ0=sQuery(id+"F0.wireOp",EDGE,"E0.bottom");var subQ1=sQuery(id+"F0.wireOp",EDGE,"E0.top");var subQ2=sQuery(id+"F0.wireOp",EDGE,"E0.left");var subQ3=sQuery(id+"F0.wireOp",EDGE,"E0.right");Q6=makeQuery(id+"F11.opFillet","BLEND_EDGE",EDGE,{"blendedFrom":[makeQuery(id+"F2.opExtrude","CAP_EDGE",EDGE,{"disambiguationData":[OSD([subQ1])],"isStart":true}),makeQuery(id+"F7.boolean.opBoolean","SPLIT",FACE,{"disambiguationData":[TD([makeQuery(id+"F2.opExtrude","SWEPT_FACE",FACE,{"disambiguationData":[OSD([subQ0])]})])],"derivedFrom":makeQuery(id+"F2.opExtrude","CAP_FACE",FACE,{"disambiguationData":[OSD([subQ0,subQ1,subQ2,subQ3])],"isStart":true})})],"blendedInto":[makeQuery(id+"F7.boolean.opBoolean","SPLIT",FACE,{"disambiguationData":[TD([makeQuery(id+"F2.opExtrude","SWEPT_FACE",FACE,{"disambiguationData":[OSD([subQ0])]})])],"derivedFrom":makeQuery(id+"F2.opExtrude","CAP_FACE",FACE,{"disambiguationData":[OSD([subQ0,subQ1,subQ2,subQ3])],"isStart":true})})]});}
            var Q7;
            Q7=makeQuery(id+"F2.opExtrude","CAP_EDGE",EDGE,{"disambiguationData":[OSD([sQuery(id+"F0.wireOp",EDGE,"E0.right")])],"isStart":true});
            fillet(context, id + "F12", {"entities" : qUnion([Q0, Q1, Q2, Q3, Q4, Q5, Q6, Q7]), "radius" : (getVariable(context, 'slot_radius')) * mm, "tangentPropagation" : true, "allowEdgeOverflow" : false});
        }
    });
